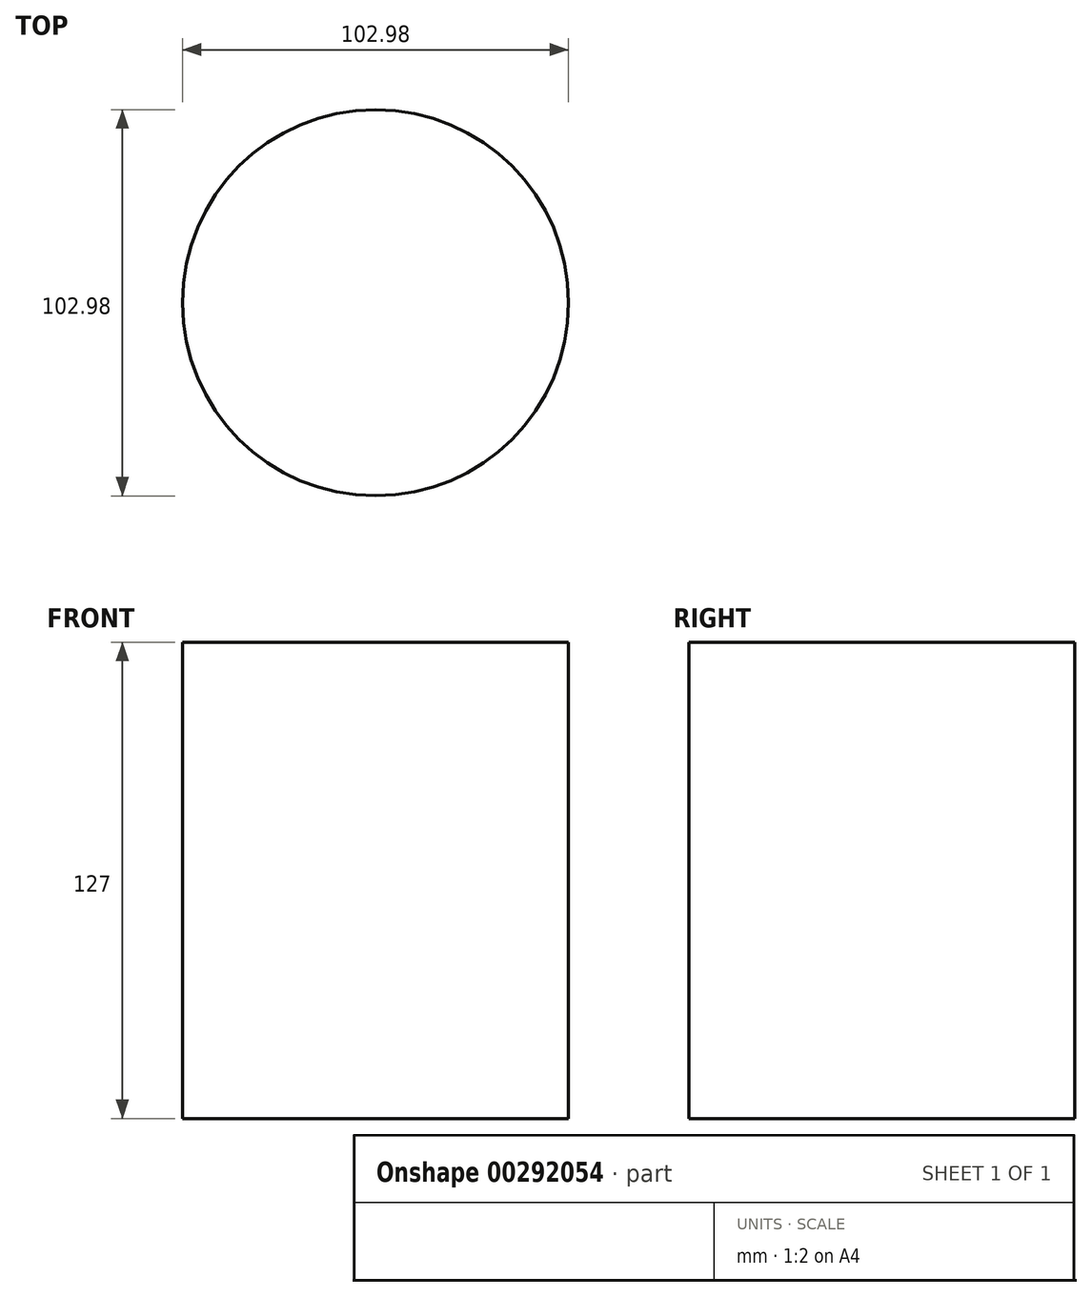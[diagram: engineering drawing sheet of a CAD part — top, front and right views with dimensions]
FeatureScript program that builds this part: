
annotation { "Feature Type Name" : "Feature", "Feature Type Description" : "" }
export const myFeature = defineFeature(function(context is Context, id is Id, definition is map)
    precondition{}
    {
        {
            var Q0;
            Q0=qCreatedBy(makeId("Top.planeOp"),FACE);
            var sketch = newSketch(context, id + "F0", { "sketchPlane" : qUnion([Q0])});
            skCircle(sketch, "E0", {"center": v(0, 0) * mm, "radius": 51.49 * mm});
            skSolve(sketch);
        }
        {
            var Q0;
            Q0=makeQuery(id+"F0.imprint","IMPRINT",FACE,{"disambiguationData":[TD([[makeQuery(id+"F0.imprint","IMPRINT",EDGE,{"derivedFrom":sQuery(id+"F0.wireOp",EDGE,"E0")}),1.0]])]});
            extrude(context, id + "F1", {"entities" : qUnion([Q0]), "depth" : 127 * mm});
        }
    });
